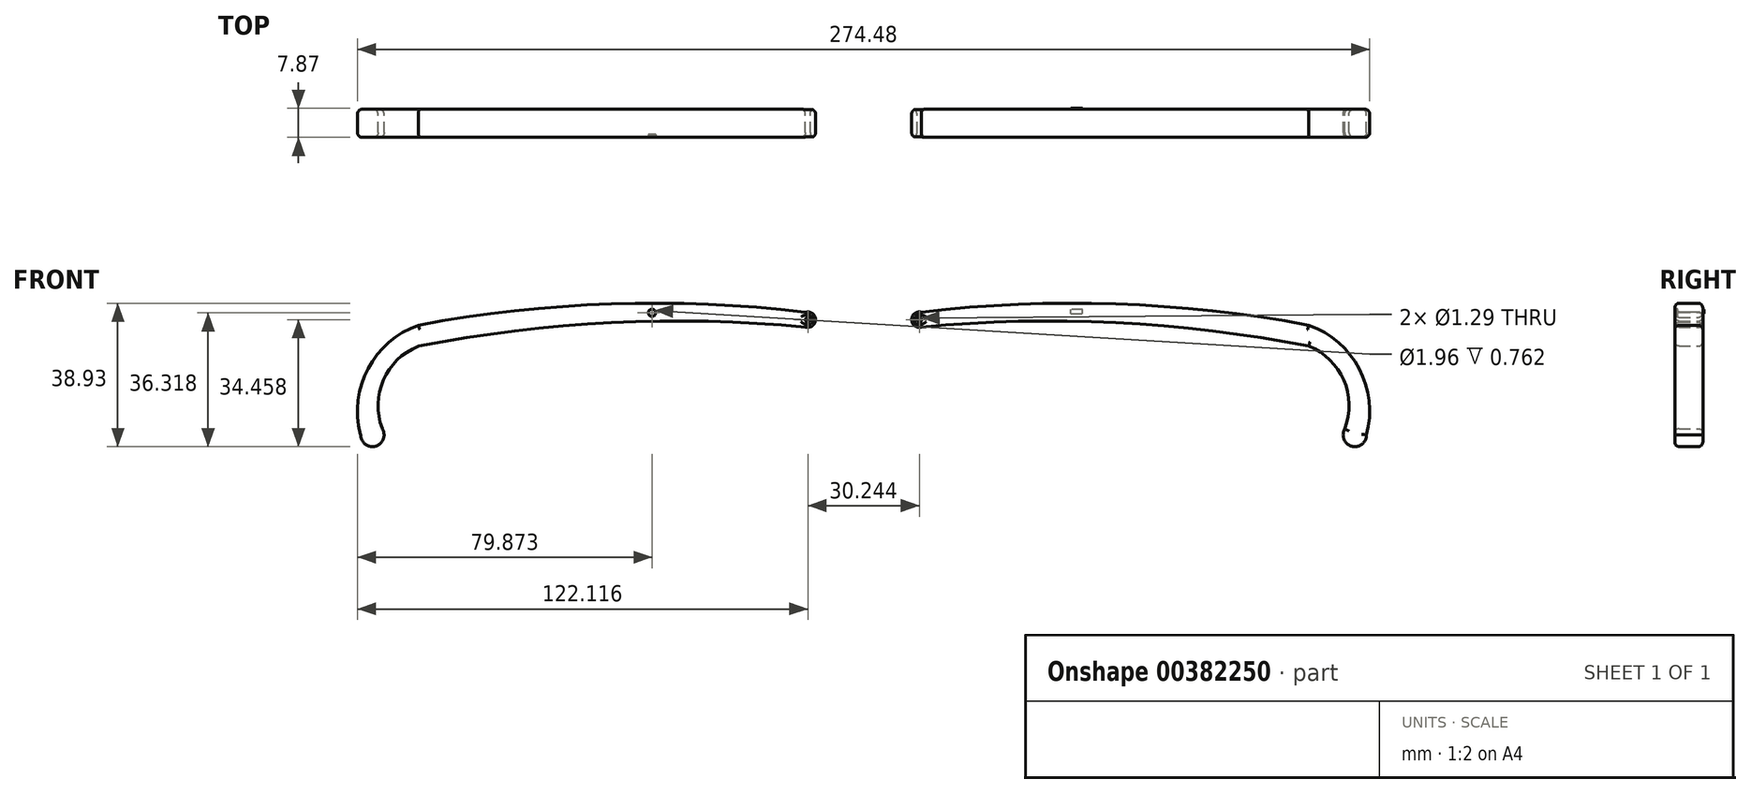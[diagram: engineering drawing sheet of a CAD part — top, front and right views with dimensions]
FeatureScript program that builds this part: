
annotation { "Feature Type Name" : "Feature", "Feature Type Description" : "" }
export const myFeature = defineFeature(function(context is Context, id is Id, definition is map)
    precondition{}
    {
        {
            var Q0;
            Q0=qCreatedBy(makeId("Front.planeOp"),FACE);
            var sketch = newSketch(context, id + "F0", { "sketchPlane" : qUnion([Q0])});
            skArc(sketch, "E0", {"start": v(60.15, 15.54) * mm, "mid": v(7.81, 21.91) * mm, "end": v(-44.9, 20.72) * mm});
            skArc(sketch, "E1", {"start": v(69.94, -6.9) * mm, "mid": v(69.66, 6.33) * mm, "end": v(60.15, 15.54) * mm});
            skArc(sketch, "E2", {"start": v(-44.9, 24.75) * mm, "mid": v(-47.53, 22.74) * mm, "end": v(-44.9, 20.72) * mm});
            skArc(sketch, "E3", {"start": v(60.15, 21.24) * mm, "mid": v(7.76, 27.02) * mm, "end": v(-44.9, 24.75) * mm});
            skArc(sketch, "E4", {"start": v(75.81, -8.53) * mm, "mid": v(73.84, 9.43) * mm, "end": v(60.15, 21.24) * mm});
            skArc(sketch, "E5", {"start": v(69.94, -6.9) * mm, "mid": v(71.8, -11.6) * mm, "end": v(75.81, -8.53) * mm});
            skArc(sketch, "E6.MirrorCS", {"start": v(-181.28, 21.24) * mm, "mid": v(-128.89, 27.02) * mm, "end": v(-76.23, 24.75) * mm});
            skArc(sketch, "E7.MirrorCS", {"start": v(-181.28, 15.54) * mm, "mid": v(-128.94, 21.91) * mm, "end": v(-76.23, 20.72) * mm});
            skArc(sketch, "E8.MirrorCS", {"start": v(-196.94, -8.53) * mm, "mid": v(-194.96, 9.43) * mm, "end": v(-181.28, 21.24) * mm});
            skArc(sketch, "E9.MirrorCS", {"start": v(-191.06, -6.9) * mm, "mid": v(-190.78, 6.33) * mm, "end": v(-181.28, 15.54) * mm});
            skArc(sketch, "E10.MirrorCS", {"start": v(-191.06, -6.9) * mm, "mid": v(-192.92, -11.6) * mm, "end": v(-196.94, -8.53) * mm});
            skArc(sketch, "E11.MirrorCS", {"start": v(-76.23, 24.75) * mm, "mid": v(-73.6, 22.74) * mm, "end": v(-76.23, 20.72) * mm});
            skCircle(sketch, "E12", {"center": v(-45.44, 22.74) * mm, "radius": 0.64 * mm});
            skCircle(sketch, "E13.MirrorC", {"center": v(-75.68, 22.74) * mm, "radius": 0.64 * mm});
            skSolve(sketch);
        }
        {
            var Q0;
            Q0 = qSketchRegion(id + "F0", true);
            extrude(context, id + "F1", {"entities" : qUnion([Q0]), "depth" : 7.62 * mm});
        }
        {
            var Q0;
            Q0=makeQuery(id+"F1.opExtrude","CAP_EDGE",EDGE,{"disambiguationData":[OSD([sQuery(id+"F0.wireOp",EDGE,"E3")])],"isStart":true});
            var Q1;
            Q1=makeQuery(id+"F1.opExtrude","CAP_EDGE",EDGE,{"disambiguationData":[OSD([sQuery(id+"F0.wireOp",EDGE,"E3")])],"isStart":false});
            var Q2;
            Q2=makeQuery(id+"F1.opExtrude","CAP_EDGE",EDGE,{"disambiguationData":[OSD([sQuery(id+"F0.wireOp",EDGE,"E2")])],"isStart":true});
            var Q3;
            Q3=makeQuery(id+"F1.opExtrude","CAP_EDGE",EDGE,{"disambiguationData":[OSD([sQuery(id+"F0.wireOp",EDGE,"E0")])],"isStart":true});
            var Q4;
            Q4=makeQuery(id+"F1.opExtrude","CAP_EDGE",EDGE,{"disambiguationData":[OSD([sQuery(id+"F0.wireOp",EDGE,"E0")])],"isStart":false});
            var Q5;
            Q5=makeQuery(id+"F1.opExtrude","CAP_EDGE",EDGE,{"disambiguationData":[OSD([sQuery(id+"F0.wireOp",EDGE,"E1")])],"isStart":false});
            var Q6;
            Q6=makeQuery(id+"F1.opExtrude","CAP_EDGE",EDGE,{"disambiguationData":[OSD([sQuery(id+"F0.wireOp",EDGE,"E1")])],"isStart":true});
            var Q7;
            Q7=makeQuery(id+"F1.opExtrude","CAP_EDGE",EDGE,{"disambiguationData":[OSD([sQuery(id+"F0.wireOp",EDGE,"E5")])],"isStart":true});
            var Q8;
            Q8=makeQuery(id+"F1.opExtrude","CAP_EDGE",EDGE,{"disambiguationData":[OSD([sQuery(id+"F0.wireOp",EDGE,"E5")])],"isStart":false});
            var Q9;
            Q9=makeQuery(id+"F1.opExtrude","CAP_EDGE",EDGE,{"disambiguationData":[OSD([sQuery(id+"F0.wireOp",EDGE,"E4")])],"isStart":true});
            var Q10;
            Q10=makeQuery(id+"F1.opExtrude","CAP_EDGE",EDGE,{"disambiguationData":[OSD([sQuery(id+"F0.wireOp",EDGE,"E4")])],"isStart":false});
            var Q11;
            Q11=makeQuery(id+"F1.opExtrude","CAP_EDGE",EDGE,{"disambiguationData":[OSD([sQuery(id+"F0.wireOp",EDGE,"E2")])],"isStart":false});
            var Q12;
            Q12=makeQuery(id+"F1.opExtrude","CAP_EDGE",EDGE,{"disambiguationData":[OSD([sQuery(id+"F0.wireOp",EDGE,"E12")])],"isStart":true});
            var Q13;
            Q13=makeQuery(id+"F1.opExtrude","CAP_EDGE",EDGE,{"disambiguationData":[OSD([sQuery(id+"F0.wireOp",EDGE,"E12")])],"isStart":false});
            fillet(context, id + "F2", {"entities" : qUnion([Q0, Q1, Q2, Q3, Q4, Q5, Q6, Q7, Q8, Q9, Q10, Q11, Q12, Q13]), "radius" : 1.27 * mm, "tangentPropagation" : true, "allowEdgeOverflow" : false});
        }
        {
            var Q0;
            Q0=makeQuery(id+"F1.opExtrude","CAP_EDGE",EDGE,{"disambiguationData":[OSD([sQuery(id+"F0.wireOp",EDGE,"E6.MirrorCS")])],"isStart":false});
            var Q1;
            Q1=makeQuery(id+"F1.opExtrude","CAP_EDGE",EDGE,{"disambiguationData":[OSD([sQuery(id+"F0.wireOp",EDGE,"E6.MirrorCS")])],"isStart":true});
            var Q2;
            Q2=makeQuery(id+"F1.opExtrude","SWEPT_FACE",FACE,{"disambiguationData":[OSD([sQuery(id+"F0.wireOp",EDGE,"E7.MirrorCS")])]});
            var Q3;
            Q3=makeQuery(id+"F1.opExtrude","CAP_EDGE",EDGE,{"disambiguationData":[OSD([sQuery(id+"F0.wireOp",EDGE,"E9.MirrorCS")])],"isStart":true});
            var Q4;
            Q4=makeQuery(id+"F1.opExtrude","CAP_EDGE",EDGE,{"disambiguationData":[OSD([sQuery(id+"F0.wireOp",EDGE,"E9.MirrorCS")])],"isStart":false});
            var Q5;
            Q5=makeQuery(id+"F1.opExtrude","CAP_EDGE",EDGE,{"disambiguationData":[OSD([sQuery(id+"F0.wireOp",EDGE,"E8.MirrorCS")])],"isStart":true});
            var Q6;
            Q6=makeQuery(id+"F1.opExtrude","CAP_EDGE",EDGE,{"disambiguationData":[OSD([sQuery(id+"F0.wireOp",EDGE,"E10.MirrorCS")])],"isStart":true});
            var Q7;
            Q7=makeQuery(id+"F1.opExtrude","CAP_EDGE",EDGE,{"disambiguationData":[OSD([sQuery(id+"F0.wireOp",EDGE,"E8.MirrorCS")])],"isStart":false});
            var Q8;
            Q8=makeQuery(id+"F1.opExtrude","SWEPT_EDGE",EDGE,{"disambiguationData":[OSD([sQuery(id+"F0.wireOp",EDGE,"E8.MirrorCS"),sQuery(id+"F0.wireOp",EDGE,"E10.MirrorCS")])]});
            var Q9;
            Q9=makeQuery(id+"F1.opExtrude","CAP_EDGE",EDGE,{"disambiguationData":[OSD([sQuery(id+"F0.wireOp",EDGE,"E10.MirrorCS")])],"isStart":false});
            var Q10;
            Q10=makeQuery(id+"F1.opExtrude","CAP_EDGE",EDGE,{"disambiguationData":[OSD([sQuery(id+"F0.wireOp",EDGE,"E7.MirrorCS")])],"isStart":false});
            var Q11;
            Q11=makeQuery(id+"F1.opExtrude","SWEPT_FACE",FACE,{"disambiguationData":[OSD([sQuery(id+"F0.wireOp",EDGE,"E10.MirrorCS")])]});
            var Q12;
            Q12=makeQuery(id+"F1.opExtrude","CAP_EDGE",EDGE,{"disambiguationData":[OSD([sQuery(id+"F0.wireOp",EDGE,"E11.MirrorCS")])],"isStart":true});
            var Q13;
            Q13=makeQuery(id+"F1.opExtrude","SWEPT_EDGE",EDGE,{"disambiguationData":[OSD([sQuery(id+"F0.wireOp",EDGE,"E7.MirrorCS"),sQuery(id+"F0.wireOp",EDGE,"E11.MirrorCS")])]});
            var Q14;
            Q14=makeQuery(id+"F1.opExtrude","CAP_FACE",FACE,{"disambiguationData":[OSD([sQuery(id+"F0.wireOp",EDGE,"E6.MirrorCS"),sQuery(id+"F0.wireOp",EDGE,"E7.MirrorCS"),sQuery(id+"F0.wireOp",EDGE,"E8.MirrorCS"),sQuery(id+"F0.wireOp",EDGE,"E9.MirrorCS"),sQuery(id+"F0.wireOp",EDGE,"E10.MirrorCS"),sQuery(id+"F0.wireOp",EDGE,"E11.MirrorCS")])],"isStart":true});
            var Q15;
            Q15=makeQuery(id+"F1.opExtrude","CAP_FACE",FACE,{"disambiguationData":[OSD([sQuery(id+"F0.wireOp",EDGE,"E6.MirrorCS"),sQuery(id+"F0.wireOp",EDGE,"E7.MirrorCS"),sQuery(id+"F0.wireOp",EDGE,"E8.MirrorCS"),sQuery(id+"F0.wireOp",EDGE,"E9.MirrorCS"),sQuery(id+"F0.wireOp",EDGE,"E10.MirrorCS"),sQuery(id+"F0.wireOp",EDGE,"E11.MirrorCS")])],"isStart":false});
            var Q16;
            Q16=makeQuery(id+"F1.opExtrude","SWEPT_FACE",FACE,{"disambiguationData":[OSD([sQuery(id+"F0.wireOp",EDGE,"E11.MirrorCS")])]});
            fillet(context, id + "F3", {"entities" : qUnion([Q0, Q1, Q2, Q3, Q4, Q5, Q6, Q7, Q8, Q9, Q10, Q11, Q12, Q13, Q14, Q15, Q16]), "radius" : 1.27 * mm, "tangentPropagation" : true, "allowEdgeOverflow" : false});
        }
        {
            var Q0;
            Q0=qCreatedBy(makeId("Front.planeOp"),FACE);
            var sketch = newSketch(context, id + "F4", { "sketchPlane" : qUnion([Q0])});
            skLineSegment(sketch, "E14", {"start": v(-1.15, 25.45) * mm, "end": v(-4.33, 25.45) * mm});
            skLineSegment(sketch, "E15", {"start": v(-4.33, 24.36) * mm, "end": v(-1.25, 24.36) * mm});
            skLineSegment(sketch, "E16", {"start": v(-1.25, 24.36) * mm, "end": v(-1.15, 25.45) * mm});
            skLineSegment(sketch, "E17", {"start": v(-4.33, 24.36) * mm, "end": v(-4.33, 25.45) * mm});
            skSolve(sketch);
        }
        {
            var Q0;
            Q0 = qSketchRegion(id + "F4", true);
            extrude(context, id + "F5", {"entities" : qUnion([Q0]), "operationType" : NewBodyOperationType.ADD, "oppositeDirection" : true, "depth" : 0.25 * mm});
        }
        {
            var Q0;
            Q0=makeQuery(id+"F1.opExtrude","CAP_FACE",FACE,{"disambiguationData":[OSD([sQuery(id+"F0.wireOp",EDGE,"E6.MirrorCS"),sQuery(id+"F0.wireOp",EDGE,"E7.MirrorCS"),sQuery(id+"F0.wireOp",EDGE,"E8.MirrorCS"),sQuery(id+"F0.wireOp",EDGE,"E9.MirrorCS"),sQuery(id+"F0.wireOp",EDGE,"E10.MirrorCS"),sQuery(id+"F0.wireOp",EDGE,"E11.MirrorCS")])],"isStart":false});
            var sketch = newSketch(context, id + "F6", { "sketchPlane" : qUnion([Q0])});
            skCircle(sketch, "E18", {"center": v(-117.93, 24.6) * mm, "radius": 0.98 * mm});
            skSolve(sketch);
        }
        {
            var Q0;
            Q0=makeQuery(id+"F6.imprint","IMPRINT",FACE,{"disambiguationData":[TD([[makeQuery(id+"F6.imprint","IMPRINT",EDGE,{"derivedFrom":sQuery(id+"F6.wireOp",EDGE,"E18")}),1.0]])]});
            extrude(context, id + "F7", {"entities" : qUnion([Q0]), "operationType" : NewBodyOperationType.REMOVE, "oppositeDirection" : true, "depth" : 0.76 * mm});
        }
    });
